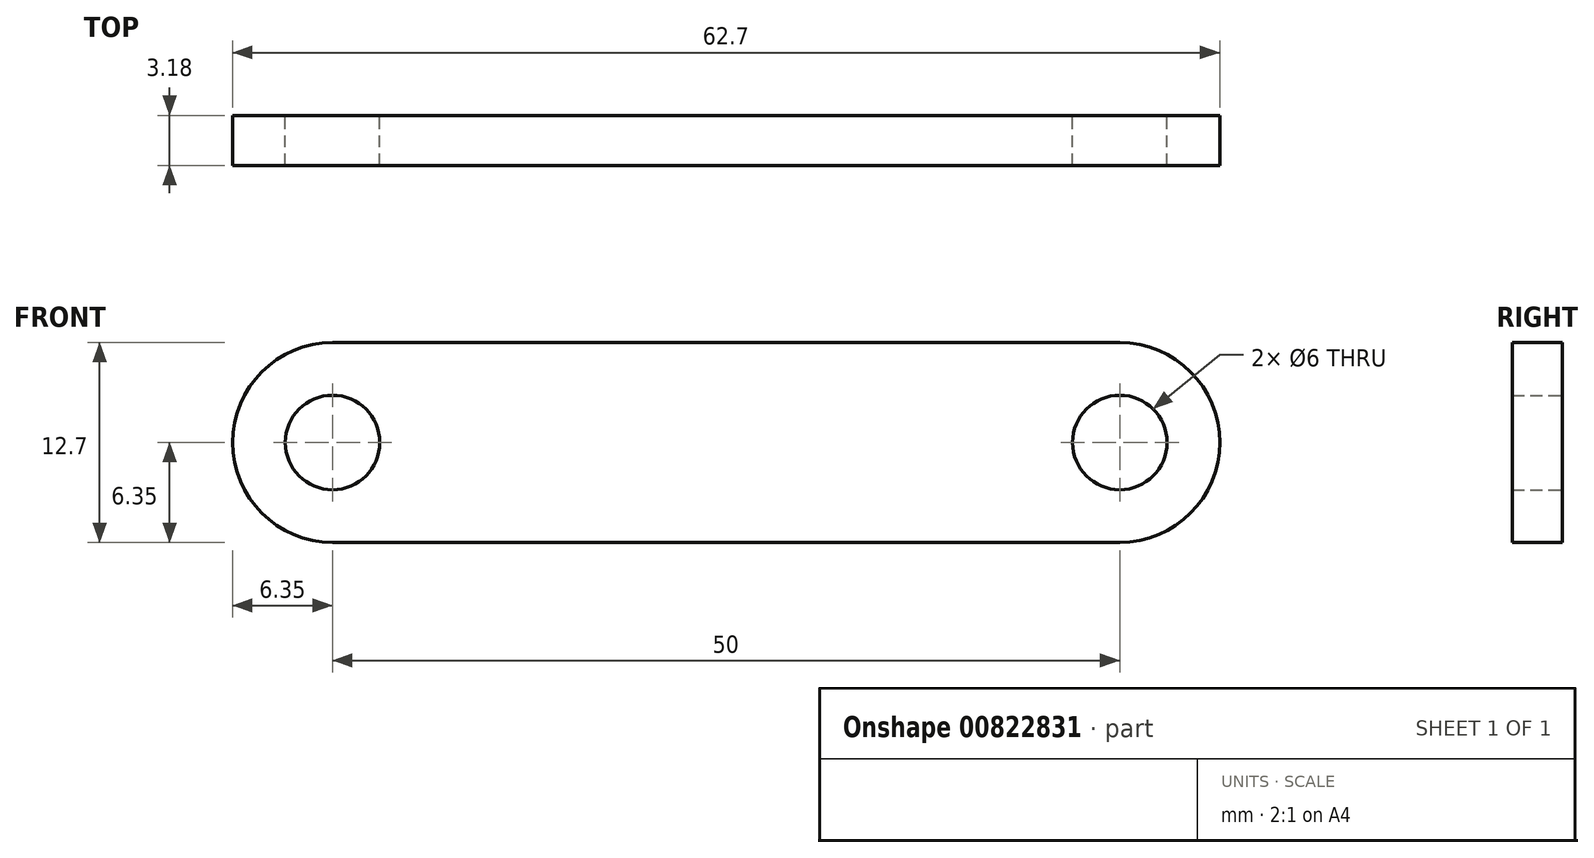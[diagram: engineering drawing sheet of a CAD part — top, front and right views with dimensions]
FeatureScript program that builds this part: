
annotation { "Feature Type Name" : "Feature", "Feature Type Description" : "" }
export const myFeature = defineFeature(function(context is Context, id is Id, definition is map)
    precondition{}
    {
        {
            var Q0;
            Q0=qCreatedBy(makeId("Front.planeOp"),FACE);
            var sketch = newSketch(context, id + "F0", { "sketchPlane" : qUnion([Q0])});
            skLineSegment(sketch, "E0", {"start": v(0, 0) * mm, "end": v(-25, 0) * mm, "construction": true});
            skArc(sketch, "E1", {"start": v(-25, 6.35) * mm, "mid": v(-31.35, 0) * mm, "end": v(-25, -6.35) * mm});
            skLineSegment(sketch, "E2", {"start": v(0, 0) * mm, "end": v(0, 38.07) * mm, "construction": true});
            skArc(sketch, "E3.MirrorC", {"start": v(25, 6.35) * mm, "mid": v(31.35, 0) * mm, "end": v(25, -6.35) * mm});
            skLineSegment(sketch, "E4", {"start": v(-25, 0) * mm, "end": v(-25, 6.35) * mm, "construction": true});
            skLineSegment(sketch, "E5", {"start": v(-25, 6.35) * mm, "end": v(25, 6.35) * mm});
            skLineSegment(sketch, "E6", {"start": v(25, 6.35) * mm, "end": v(25, -6.35) * mm, "construction": true});
            skLineSegment(sketch, "E7", {"start": v(25, -6.35) * mm, "end": v(-25, -6.35) * mm});
            skCircle(sketch, "E8", {"center": v(-25, 0) * mm, "radius": 3 * mm});
            skCircle(sketch, "E9.MirrorC", {"center": v(25, 0) * mm, "radius": 3 * mm});
            skCircle(sketch, "E10", {"center": v(0, 0) * mm, "radius": 3 * mm, "construction": true});
            skSolve(sketch);
        }
        {
            var Q0;
            Q0=qSketchRegion(id+"F0",true);
            extrude(context, id + "F1", {"entities" : qUnion([Q0]), "depth" : (25.4 / 8) * mm, "offsetDistance" : 25 * mm});
        }
    });
